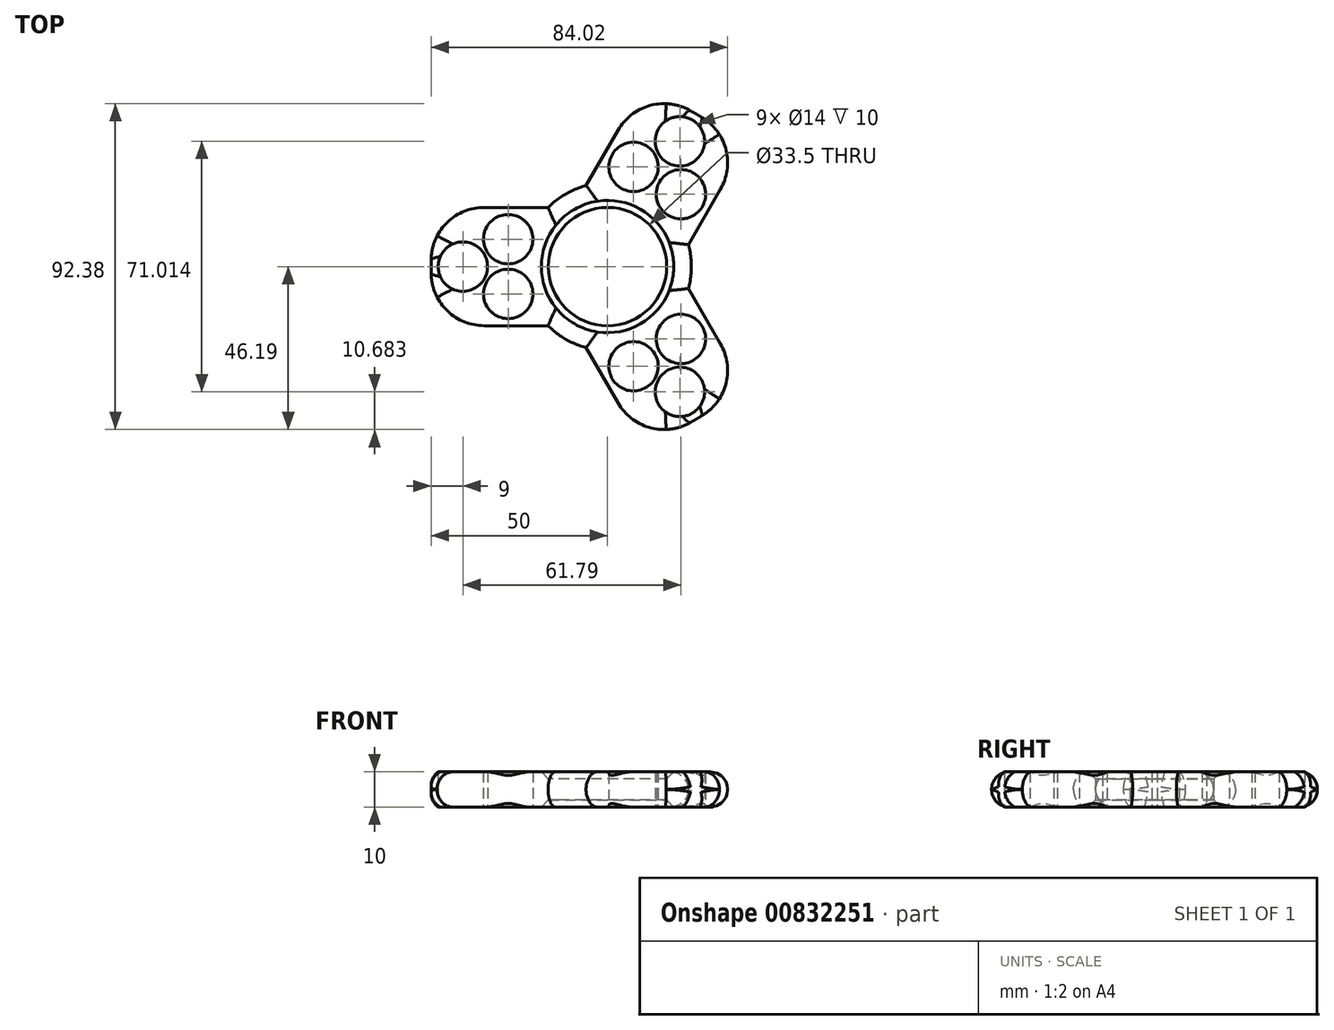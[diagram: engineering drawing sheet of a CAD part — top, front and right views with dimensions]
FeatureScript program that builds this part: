
annotation { "Feature Type Name" : "Feature", "Feature Type Description" : "" }
export const myFeature = defineFeature(function(context is Context, id is Id, definition is map)
    precondition{}
    {
        {
            var Q0;
            Q0=qCreatedBy(makeId("Top.planeOp"),FACE);
            var sketch = newSketch(context, id + "F0", { "sketchPlane" : qUnion([Q0])});
            skCircle(sketch, "E0", {"center": v(0, 0) * mm, "radius": 16.75 * mm});
            skCircle(sketch, "E1", {"center": v(0, 0) * mm, "radius": 23.75 * mm});
            skSolve(sketch);
        }
        {
            var Q0;
            Q0=makeQuery(id+"F0.imprint","IMPRINT",FACE,{"disambiguationData":[TD([[makeQuery(id+"F0.imprint","IMPRINT",EDGE,{"derivedFrom":sQuery(id+"F0.wireOp",EDGE,"E0")}),-1.0]])]});
            var sketch = newSketch(context, id + "F1", { "sketchPlane" : qUnion([Q0])});
            skCircle(sketch, "E2", {"center": v(0, 0) * mm, "radius": 23.75 * mm, "construction": true});
            skCircle(sketch, "E3", {"center": v(0, 0) * mm, "radius": 16.75 * mm, "construction": true});
            skLineSegment(sketch, "E4.bottom", {"start": v(0, 16.75) * mm, "end": v(-35, 16.75) * mm});
            skLineSegment(sketch, "E4.top", {"start": v(0, -16.75) * mm, "end": v(-35, -16.75) * mm});
            skLineSegment(sketch, "E4.left", {"start": v(0, 16.75) * mm, "end": v(0, -16.75) * mm});
            skLineSegment(sketch, "E4.right", {"start": v(-50, 1.75) * mm, "end": v(-50, -1.75) * mm});
            skPoint(sketch, "E5.visualSharp", {"position": v(-50, 16.75) * mm});
            skArc(sketch, "E5.filletArc", {"start": v(-35, 16.75) * mm, "mid": v(-45.6, 12.36) * mm, "end": v(-50, 1.75) * mm});
            skPoint(sketch, "E6.visualSharp", {"position": v(-50, -16.75) * mm});
            skArc(sketch, "E6.filletArc", {"start": v(-50, -1.75) * mm, "mid": v(-45.6, -12.36) * mm, "end": v(-35, -16.75) * mm});
            skCircle(sketch, "E7", {"center": v(-41, 0) * mm, "radius": 7 * mm});
            skCircle(sketch, "E8", {"center": v(-28.16, 7.75) * mm, "radius": 7 * mm});
            skCircle(sketch, "E9", {"center": v(-28.16, -7.75) * mm, "radius": 7 * mm});
            skLineSegment(sketch, "E10.1.0", {"start": v(-14.5, -8.38) * mm, "end": v(3, -38.69) * mm});
            skArc(sketch, "E10.1.1", {"start": v(3, -38.69) * mm, "mid": v(12.1, -45.67) * mm, "end": v(23.48, -44.18) * mm});
            skArc(sketch, "E10.1.2", {"start": v(26.52, -42.43) * mm, "mid": v(33.5, -33.32) * mm, "end": v(32, -21.94) * mm});
            skCircle(sketch, "E10.1.3", {"center": v(20.5, -35.5) * mm, "radius": 7 * mm});
            skCircle(sketch, "E10.1.4", {"center": v(20.8, -20.5) * mm, "radius": 7 * mm});
            skCircle(sketch, "E10.1.5", {"center": v(7.37, -28.26) * mm, "radius": 7 * mm});
            skLineSegment(sketch, "E10.1.6", {"start": v(14.5, 8.37) * mm, "end": v(32, -21.94) * mm});
            skLineSegment(sketch, "E10.1.7", {"start": v(-14.5, -8.38) * mm, "end": v(14.5, 8.38) * mm});
            skLineSegment(sketch, "E10.1.8", {"start": v(23.48, -44.18) * mm, "end": v(26.52, -42.43) * mm});
            skLineSegment(sketch, "E10.2.0", {"start": v(14.5, -8.38) * mm, "end": v(32, 21.94) * mm});
            skArc(sketch, "E10.2.1", {"start": v(32, 21.94) * mm, "mid": v(33.5, 33.32) * mm, "end": v(26.52, 42.43) * mm});
            skArc(sketch, "E10.2.2", {"start": v(23.48, 44.18) * mm, "mid": v(12.1, 45.67) * mm, "end": v(3, 38.69) * mm});
            skCircle(sketch, "E10.2.3", {"center": v(20.5, 35.5) * mm, "radius": 7 * mm});
            skCircle(sketch, "E10.2.4", {"center": v(7.37, 28.26) * mm, "radius": 7 * mm});
            skCircle(sketch, "E10.2.5", {"center": v(20.8, 20.5) * mm, "radius": 7 * mm});
            skLineSegment(sketch, "E10.2.6", {"start": v(-14.5, 8.37) * mm, "end": v(3, 38.69) * mm});
            skLineSegment(sketch, "E10.2.7", {"start": v(14.5, -8.38) * mm, "end": v(-14.5, 8.38) * mm});
            skLineSegment(sketch, "E10.2.8", {"start": v(26.52, 42.43) * mm, "end": v(23.48, 44.18) * mm});
            skSolve(sketch);
        }
        {
            var Q0;
            Q0=makeQuery(id+"F0.imprint","IMPRINT",FACE,{"disambiguationData":[TD([[makeQuery(id+"F0.imprint","IMPRINT",EDGE,{"derivedFrom":sQuery(id+"F0.wireOp",EDGE,"E0")}),-1.0]])]});
            extrude(context, id + "F2", {"entities" : qUnion([Q0]), "depth" : 10 * mm, "offsetDistance" : 25 * mm});
        }
        {
            var Q0;
            Q0=makeQuery(id+"F1.imprint","IMPRINT",FACE,{"disambiguationData":[TD([[makeQuery(id+"F1.imprint","IMPRINT",EDGE,{"derivedFrom":sQuery(id+"F1.wireOp",EDGE,"E4.right")}),1.0]])]});
            var Q1;
            Q1=makeQuery(id+"F1.imprint","IMPRINT",FACE,{"disambiguationData":[TD([[makeQuery(id+"F1.imprint","IMPRINT",EDGE,{"derivedFrom":sQuery(id+"F1.wireOp",EDGE,"E9")}),1.0]])]});
            var Q2;
            {var subQ0=sQuery(id+"F1.wireOp",EDGE,"E7");var subQ1=makeQuery(id+"F1.imprint","INTERSECT",VERTEX,{"derivedFrom":[subQ0,sQuery(id+"F1.wireOp",EDGE,"E8")]});Q2=makeQuery(id+"F1.imprint","IMPRINT",FACE,{"disambiguationData":[TD([[makeQuery(id+"F1.imprint","IMPRINT",EDGE,{"disambiguationData":[TD([[subQ1,-1.0]])],"derivedFrom":subQ0}),1.0]])]});}
            var Q3;
            Q3=makeQuery(id+"F1.imprint","IMPRINT",FACE,{"disambiguationData":[TD([[makeQuery(id+"F1.imprint","IMPRINT",EDGE,{"derivedFrom":sQuery(id+"F1.wireOp",EDGE,"E8")}),1.0]])]});
            var Q4;
            {var subQ6=sQuery(id+"F1.wireOp",EDGE,"E10.1.1");Q4=makeQuery(id+"F1.imprint","IMPRINT",FACE,{"disambiguationData":[TD([[makeQuery(id+"F1.imprint","IMPRINT",EDGE,{"derivedFrom":subQ6}),1.0]])]});}
            var Q5;
            Q5=makeQuery(id+"F1.imprint","IMPRINT",FACE,{"disambiguationData":[TD([[makeQuery(id+"F1.imprint","IMPRINT",EDGE,{"derivedFrom":sQuery(id+"F1.wireOp",EDGE,"E10.1.5")}),1.0]])]});
            var Q6;
            Q6=makeQuery(id+"F1.imprint","IMPRINT",FACE,{"disambiguationData":[TD([[makeQuery(id+"F1.imprint","IMPRINT",EDGE,{"derivedFrom":sQuery(id+"F1.wireOp",EDGE,"E10.1.4")}),1.0]])]});
            var Q7;
            {var subQ0=sQuery(id+"F1.wireOp",EDGE,"E10.1.3");var subQ1=makeQuery(id+"F1.imprint","INTERSECT",VERTEX,{"derivedFrom":[subQ0,sQuery(id+"F1.wireOp",EDGE,"E10.1.4")]});Q7=makeQuery(id+"F1.imprint","IMPRINT",FACE,{"disambiguationData":[TD([[makeQuery(id+"F1.imprint","IMPRINT",EDGE,{"disambiguationData":[TD([[subQ1,1.0]])],"derivedFrom":subQ0}),1.0]])]});}
            var Q8;
            Q8=makeQuery(id+"F1.imprint","IMPRINT",FACE,{"disambiguationData":[TD([[makeQuery(id+"F1.imprint","IMPRINT",EDGE,{"derivedFrom":sQuery(id+"F1.wireOp",EDGE,"E10.2.5")}),1.0]])]});
            var Q9;
            Q9=makeQuery(id+"F1.imprint","IMPRINT",FACE,{"disambiguationData":[TD([[makeQuery(id+"F1.imprint","IMPRINT",EDGE,{"derivedFrom":sQuery(id+"F1.wireOp",EDGE,"E10.2.4")}),1.0]])]});
            var Q10;
            {var subQ0=sQuery(id+"F1.wireOp",EDGE,"E10.2.3");var subQ1=makeQuery(id+"F1.imprint","INTERSECT",VERTEX,{"derivedFrom":[subQ0,sQuery(id+"F1.wireOp",EDGE,"E10.2.4")]});Q10=makeQuery(id+"F1.imprint","IMPRINT",FACE,{"disambiguationData":[TD([[makeQuery(id+"F1.imprint","IMPRINT",EDGE,{"disambiguationData":[TD([[subQ1,1.0]])],"derivedFrom":subQ0}),1.0]])]});}
            var Q11;
            {var subQ11=sQuery(id+"F1.wireOp",EDGE,"E10.2.1");Q11=makeQuery(id+"F1.imprint","IMPRINT",FACE,{"disambiguationData":[TD([[makeQuery(id+"F1.imprint","IMPRINT",EDGE,{"derivedFrom":subQ11}),1.0]])]});}
            extrude(context, id + "F3", {"entities" : qUnion([Q0, Q1, Q2, Q3, Q4, Q5, Q6, Q7, Q8, Q9, Q10, Q11]), "operationType" : NewBodyOperationType.ADD, "depth" : 10 * mm, "offsetDistance" : 25 * mm});
        }
        {
            var Q0;
            {var subQ0=sQuery(id+"F1.wireOp",EDGE,"E7");var subQ1=makeQuery(id+"F1.imprint","INTERSECT",VERTEX,{"derivedFrom":[subQ0,sQuery(id+"F1.wireOp",EDGE,"E8")]});Q0=makeQuery(id+"F1.imprint","IMPRINT",FACE,{"disambiguationData":[TD([[makeQuery(id+"F1.imprint","IMPRINT",EDGE,{"disambiguationData":[TD([[subQ1,-1.0]])],"derivedFrom":subQ0}),1.0]])]});}
            var Q1;
            {var subQ0=sQuery(id+"F1.wireOp",EDGE,"E10.1.3");var subQ1=makeQuery(id+"F1.imprint","INTERSECT",VERTEX,{"derivedFrom":[subQ0,sQuery(id+"F1.wireOp",EDGE,"E10.1.4")]});Q1=makeQuery(id+"F1.imprint","IMPRINT",FACE,{"disambiguationData":[TD([[makeQuery(id+"F1.imprint","IMPRINT",EDGE,{"disambiguationData":[TD([[subQ1,1.0]])],"derivedFrom":subQ0}),1.0]])]});}
            var Q2;
            {var subQ0=sQuery(id+"F1.wireOp",EDGE,"E10.2.3");var subQ1=makeQuery(id+"F1.imprint","INTERSECT",VERTEX,{"derivedFrom":[subQ0,sQuery(id+"F1.wireOp",EDGE,"E10.2.4")]});Q2=makeQuery(id+"F1.imprint","IMPRINT",FACE,{"disambiguationData":[TD([[makeQuery(id+"F1.imprint","IMPRINT",EDGE,{"disambiguationData":[TD([[subQ1,1.0]])],"derivedFrom":subQ0}),1.0]])]});}
            var Q3;
            Q3=makeQuery(id+"F1.imprint","IMPRINT",FACE,{"disambiguationData":[TD([[makeQuery(id+"F1.imprint","IMPRINT",EDGE,{"derivedFrom":sQuery(id+"F1.wireOp",EDGE,"E9")}),1.0]])]});
            var Q4;
            Q4=makeQuery(id+"F1.imprint","IMPRINT",FACE,{"disambiguationData":[TD([[makeQuery(id+"F1.imprint","IMPRINT",EDGE,{"derivedFrom":sQuery(id+"F1.wireOp",EDGE,"E8")}),1.0]])]});
            var Q5;
            Q5=makeQuery(id+"F1.imprint","IMPRINT",FACE,{"disambiguationData":[TD([[makeQuery(id+"F1.imprint","IMPRINT",EDGE,{"derivedFrom":sQuery(id+"F1.wireOp",EDGE,"E10.2.4")}),1.0]])]});
            var Q6;
            Q6=makeQuery(id+"F1.imprint","IMPRINT",FACE,{"disambiguationData":[TD([[makeQuery(id+"F1.imprint","IMPRINT",EDGE,{"derivedFrom":sQuery(id+"F1.wireOp",EDGE,"E10.2.5")}),1.0]])]});
            var Q7;
            Q7=makeQuery(id+"F1.imprint","IMPRINT",FACE,{"disambiguationData":[TD([[makeQuery(id+"F1.imprint","IMPRINT",EDGE,{"derivedFrom":sQuery(id+"F1.wireOp",EDGE,"E10.1.4")}),1.0]])]});
            var Q8;
            Q8=makeQuery(id+"F1.imprint","IMPRINT",FACE,{"disambiguationData":[TD([[makeQuery(id+"F1.imprint","IMPRINT",EDGE,{"derivedFrom":sQuery(id+"F1.wireOp",EDGE,"E10.1.5")}),1.0]])]});
            extrude(context, id + "F4", {"entities" : qUnion([Q0, Q1, Q2, Q3, Q4, Q5, Q6, Q7, Q8]), "operationType" : NewBodyOperationType.REMOVE, "endBound" : BoundingType.THROUGH_ALL, "depth" : 63.6 * mm, "offsetDistance" : 25 * mm});
        }
        {
            var Q0;
            Q0=makeQuery(id+"F3.opExtrude","CAP_EDGE",EDGE,{"disambiguationData":[OSD([sQuery(id+"F1.wireOp",EDGE,"E4.top")])],"isStart":false});
            var Q1;
            Q1=makeQuery(id+"F3.opExtrude","CAP_EDGE",EDGE,{"disambiguationData":[OSD([sQuery(id+"F1.wireOp",EDGE,"E10.2.6")])],"isStart":false});
            var Q2;
            Q2=makeQuery(id+"F3.opExtrude","CAP_EDGE",EDGE,{"disambiguationData":[OSD([sQuery(id+"F1.wireOp",EDGE,"E10.1.0")])],"isStart":false});
            var Q3;
            {var subQ0=sQuery(id+"F1.wireOp",EDGE,"E4.top");var subQ1=sQuery(id+"F0.wireOp",EDGE,"E1");Q3=makeQuery(id+"F3.boolean.opBoolean","SPLIT",EDGE,{"disambiguationData":[TD([makeQuery(id+"F3.opExtrude","SWEPT_FACE",FACE,{"disambiguationData":[OSD([subQ0])]})])],"derivedFrom":makeQuery(id+"F2.opExtrude","CAP_EDGE",EDGE,{"disambiguationData":[OSD([subQ1])],"isStart":false})});}
            var Q4;
            {var subQ0=sQuery(id+"F1.wireOp",EDGE,"E10.1.6");var subQ1=sQuery(id+"F0.wireOp",EDGE,"E1");Q4=makeQuery(id+"F3.boolean.opBoolean","SPLIT",EDGE,{"disambiguationData":[TD([makeQuery(id+"F3.opExtrude","SWEPT_FACE",FACE,{"disambiguationData":[OSD([subQ0])]})])],"derivedFrom":makeQuery(id+"F2.opExtrude","CAP_EDGE",EDGE,{"disambiguationData":[OSD([subQ1])],"isStart":false})});}
            var Q5;
            {var subQ0=sQuery(id+"F1.wireOp",EDGE,"E4.bottom");var subQ1=sQuery(id+"F0.wireOp",EDGE,"E1");Q5=makeQuery(id+"F3.boolean.opBoolean","SPLIT",EDGE,{"disambiguationData":[TD([makeQuery(id+"F3.opExtrude","SWEPT_FACE",FACE,{"disambiguationData":[OSD([subQ0])]})])],"derivedFrom":makeQuery(id+"F2.opExtrude","CAP_EDGE",EDGE,{"disambiguationData":[OSD([subQ1])],"isStart":false})});}
            var Q6;
            {var subQ0=sQuery(id+"F1.wireOp",EDGE,"E4.top");var subQ1=sQuery(id+"F0.wireOp",EDGE,"E1");Q6=makeQuery(id+"F3.boolean.opBoolean","SPLIT",EDGE,{"disambiguationData":[TD([makeQuery(id+"F3.opExtrude","SWEPT_FACE",FACE,{"disambiguationData":[OSD([subQ0])]})])],"derivedFrom":makeQuery(id+"F2.opExtrude","CAP_EDGE",EDGE,{"disambiguationData":[OSD([subQ1])],"isStart":true})});}
            var Q7;
            Q7=makeQuery(id+"F3.opExtrude","CAP_EDGE",EDGE,{"disambiguationData":[OSD([sQuery(id+"F1.wireOp",EDGE,"E4.top")])],"isStart":true});
            var Q8;
            Q8=makeQuery(id+"F3.opExtrude","CAP_EDGE",EDGE,{"disambiguationData":[OSD([sQuery(id+"F1.wireOp",EDGE,"E10.1.0")])],"isStart":true});
            var Q9;
            {var subQ0=sQuery(id+"F1.wireOp",EDGE,"E10.1.6");var subQ1=sQuery(id+"F0.wireOp",EDGE,"E1");Q9=makeQuery(id+"F3.boolean.opBoolean","SPLIT",EDGE,{"disambiguationData":[TD([makeQuery(id+"F3.opExtrude","SWEPT_FACE",FACE,{"disambiguationData":[OSD([subQ0])]})])],"derivedFrom":makeQuery(id+"F2.opExtrude","CAP_EDGE",EDGE,{"disambiguationData":[OSD([subQ1])],"isStart":true})});}
            var Q10;
            Q10=makeQuery(id+"F3.opExtrude","CAP_EDGE",EDGE,{"disambiguationData":[OSD([sQuery(id+"F1.wireOp",EDGE,"E10.2.0")])],"isStart":true});
            var Q11;
            {var subQ0=sQuery(id+"F1.wireOp",EDGE,"E4.bottom");var subQ1=sQuery(id+"F0.wireOp",EDGE,"E1");Q11=makeQuery(id+"F3.boolean.opBoolean","SPLIT",EDGE,{"disambiguationData":[TD([makeQuery(id+"F3.opExtrude","SWEPT_FACE",FACE,{"disambiguationData":[OSD([subQ0])]})])],"derivedFrom":makeQuery(id+"F2.opExtrude","CAP_EDGE",EDGE,{"disambiguationData":[OSD([subQ1])],"isStart":true})});}
            fillet(context, id + "F5", {"entities" : qUnion([Q0, Q1, Q2, Q3, Q4, Q5, Q6, Q7, Q8, Q9, Q10, Q11]), "radius" : 5 * mm, "tangentPropagation" : true, "allowEdgeOverflow" : false});
        }
        {
            var Q0;
            Q0=makeQuery(id+"F2.opExtrude","CAP_EDGE",EDGE,{"disambiguationData":[OSD([sQuery(id+"F0.wireOp",EDGE,"E0")])],"isStart":true});
            var Q1;
            Q1=makeQuery(id+"F2.opExtrude","CAP_EDGE",EDGE,{"disambiguationData":[OSD([sQuery(id+"F0.wireOp",EDGE,"E0")])],"isStart":false});
            chamfer(context, id + "F6", {"entities" : qUnion([Q0, Q1]), "width" : 2 * mm, "tangentPropagation" : true});
        }
    });
